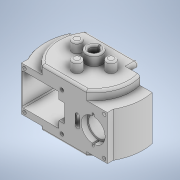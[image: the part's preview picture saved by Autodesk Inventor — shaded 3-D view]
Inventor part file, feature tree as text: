
AUTODESK INVENTOR PART (.ipt)
format: ipt  version: 2021 (Build 250183000, 183)  size: 878,080 bytes
history: native  units: mm
features: extrude x31, sketch x25, fillet x8, other x1, loft x1
ambient origin geometry x8: Origin, YZ Plane, XZ Plane, XY Plane, X Axis, Y Axis, Z Axis, Center Point
bodies: Body1 (feature_tree)
feature tree (66):
  other  "Bryła1"
  extrude  "Wyciągnięcie proste1"  Depth=86.5mm
  extrude  "Wyciągnięcie proste3"  Depth=30.0mm
  extrude  "Wyciągnięcie proste4"  Depth=40.0mm TaperAngle=0.0deg
  extrude  "Wyciągnięcie proste9"  Depth=43.25mm
  fillet  "Zaokrąglenie1"  Radius=8.0mm
  extrude  "Wyciągnięcie proste11"  Depth=43.25mm
  extrude  "Wyciągnięcie proste12"  Depth=9.0mm
  extrude  "Wyciągnięcie proste13"  Depth=3.0mm TaperAngle=0.0deg
  extrude  "Wyciągnięcie proste16"  Depth=9.0mm
  extrude  "Wyciągnięcie proste18"  Depth=15.0mm
  extrude  "Wyciągnięcie proste19"  Depth=30.0mm
  extrude  "Wyciągnięcie proste20"  Depth=14.0mm
  extrude  "Wyciągnięcie proste21"  Depth=8.0mm
  extrude  "Wyciągnięcie proste22"  Depth=8.0mm
  fillet  "Zaokrąglenie2"  Radius=8.0mm
  extrude  "Wyciągnięcie proste24"  Depth=9.0mm TaperAngle=0.0deg
  sketch  "Szkic51"
  extrude  "Wyciągnięcie proste25"  Depth=1.5mm
  extrude  "Wyciągnięcie proste27"  TaperAngle=0.0deg  [1 undecoded]
  extrude  "Wyciągnięcie proste28"  Depth=65.0mm
  extrude  "Wyciągnięcie proste29"  Depth=8.0mm TaperAngle=0.0deg
  extrude  "Wyciągnięcie proste30"  Depth=65.0mm
  extrude  "Wyciągnięcie proste33"  Depth=4.0mm TaperAngle=0.0deg
  extrude  "Wyciągnięcie proste34"  Depth=18.0mm
  fillet  "Zaokrąglenie4"  [1 undecoded]
  extrude  "Wyciągnięcie proste35"  Depth=21.0mm
  extrude  "Wyciągnięcie proste36"  Depth=5.0mm TaperAngle=0.0deg
  extrude  "Wyciągnięcie proste37"  Depth=5.0mm TaperAngle=0.0deg
  extrude  "Wyciągnięcie proste38"  Depth=21.0mm
  sketch  "Szkic93"
  extrude  "Wyciągnięcie proste39"  TaperAngle=0.0deg  [1 undecoded]
  extrude  "Wyciągnięcie proste40"  Depth=21.0mm
  fillet  "Zaokrąglenie5"  Radius=5.0mm
  fillet  "Zaokrąglenie6"  Radius=15.0mm
  fillet  "Zaokrąglenie7"  Radius=8.0mm
  fillet  "Zaokrąglenie8"  Radius=9.0mm
  extrude  "Wyciągnięcie proste41"  Depth=1.5mm
  extrude  "Wyciągnięcie proste42"  Depth=65.0mm
  extrude  "Wyciągnięcie proste43"  Depth=4.0mm TaperAngle=0.0deg
  fillet  "Zaokrąglenie10"  Radius=37.0mm
  sketch  "Szkic117"
  sketch  "Szkic120"
  loft  "Wyciągnięcie złożone1"
  extrude  "Wyciągnięcie proste48"  Depth=45.0mm
  sketch  "Szkic1"
  sketch  "Szkic15"
  sketch  "Szkic37"
  sketch  "Szkic41"
  sketch  "Szkic43"
  sketch  "Szkic54"
  sketch  "Szkic55"
  sketch  "Szkic56"
  sketch  "Szkic58"
  sketch  "Szkic78"
  sketch  "Szkic80"
  sketch  "Szkic81"
  sketch  "Szkic82"
  sketch  "Szkic91"
  sketch  "Szkic92"
  sketch  "Szkic95"
  sketch  "Szkic97"
  sketch  "Szkic101"
  sketch  "Szkic103"
  sketch  "Szkic123"
  sketch  "Szkic39"
note: 3 required parameter values undecoded (feature->parameter linkage not recoverable at this tier; creation-order binding heuristic only, values carry confidence <= 0.55)
